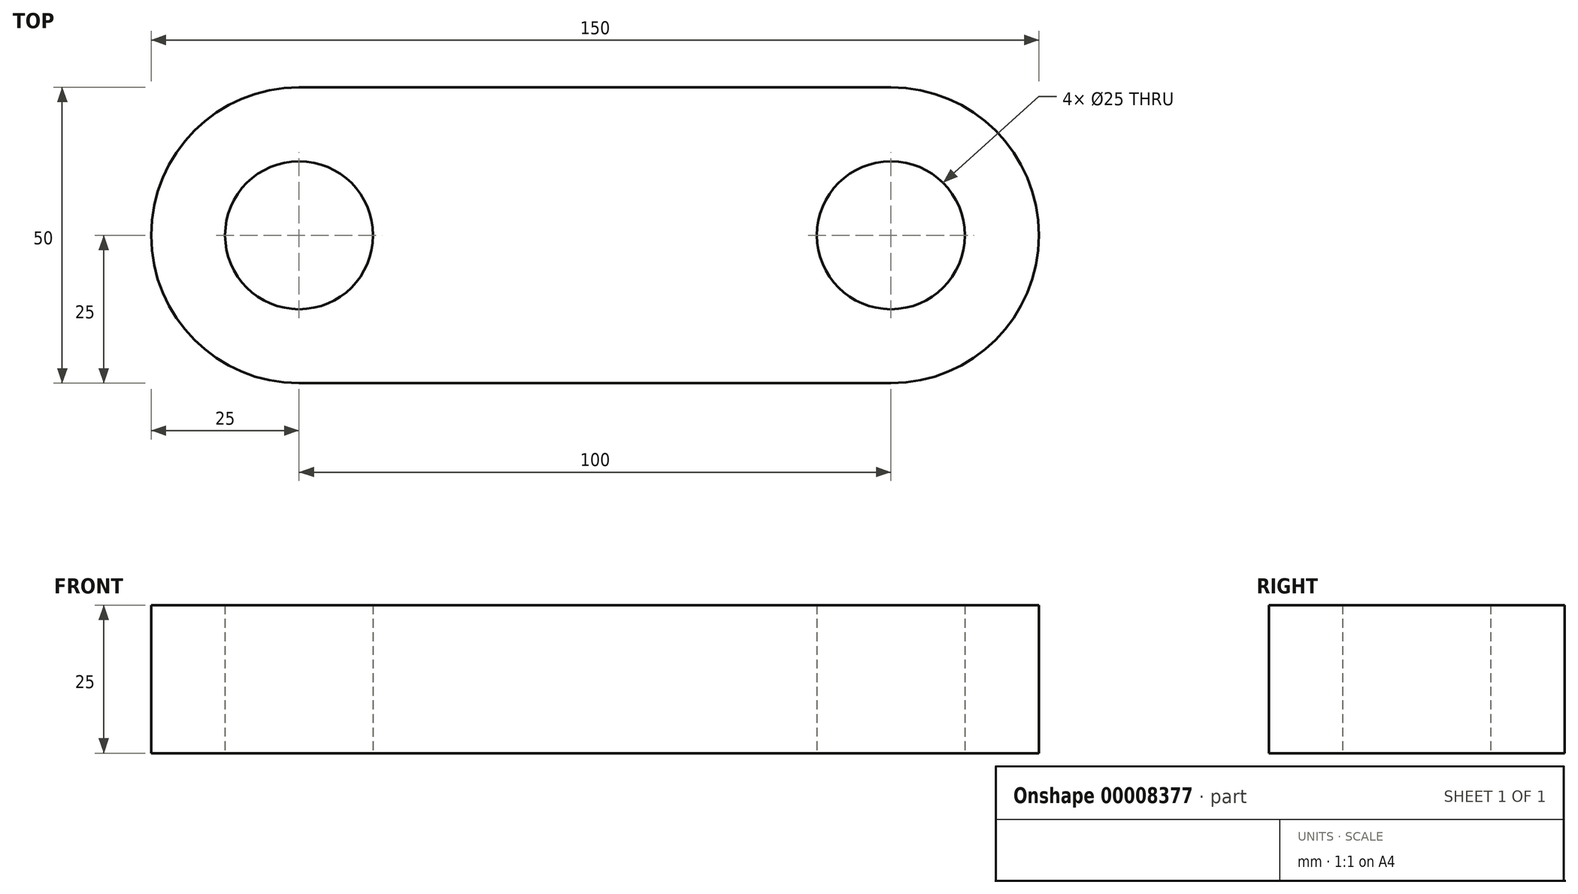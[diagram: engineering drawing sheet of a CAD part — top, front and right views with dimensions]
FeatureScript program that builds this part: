
annotation { "Feature Type Name" : "Feature", "Feature Type Description" : "" }
export const myFeature = defineFeature(function(context is Context, id is Id, definition is map)
    precondition{}
    {
        {
            var Q0;
            Q0=qCreatedBy(makeId("Top.planeOp"),FACE);
            var sketch = newSketch(context, id + "F0", { "sketchPlane" : qUnion([Q0])});
            skLineSegment(sketch, "E0.rect.bottom", {"start": v(50, 25) * mm, "end": v(-50, 25) * mm});
            skLineSegment(sketch, "E0.rect.top", {"start": v(50, -25) * mm, "end": v(-50, -25) * mm});
            skPoint(sketch, "E0.rect.middle", {"position": v(0, 0) * mm});
            skArc(sketch, "E1", {"start": v(-50, 25) * mm, "mid": v(-75, 0) * mm, "end": v(-50, -25) * mm});
            skArc(sketch, "E2", {"start": v(50, -25) * mm, "mid": v(75, 0) * mm, "end": v(50, 25) * mm});
            skCircle(sketch, "E3", {"center": v(-50, 0) * mm, "radius": 12.5 * mm});
            skCircle(sketch, "E4", {"center": v(50, 0) * mm, "radius": 12.5 * mm});
            skSolve(sketch);
        }
        {
            var Q0;
            Q0 = qSketchRegion(id + "F0", true);
            extrude(context, id + "F1", {"entities" : qUnion([Q0]), "depth" : 25 * mm});
        }
    });
